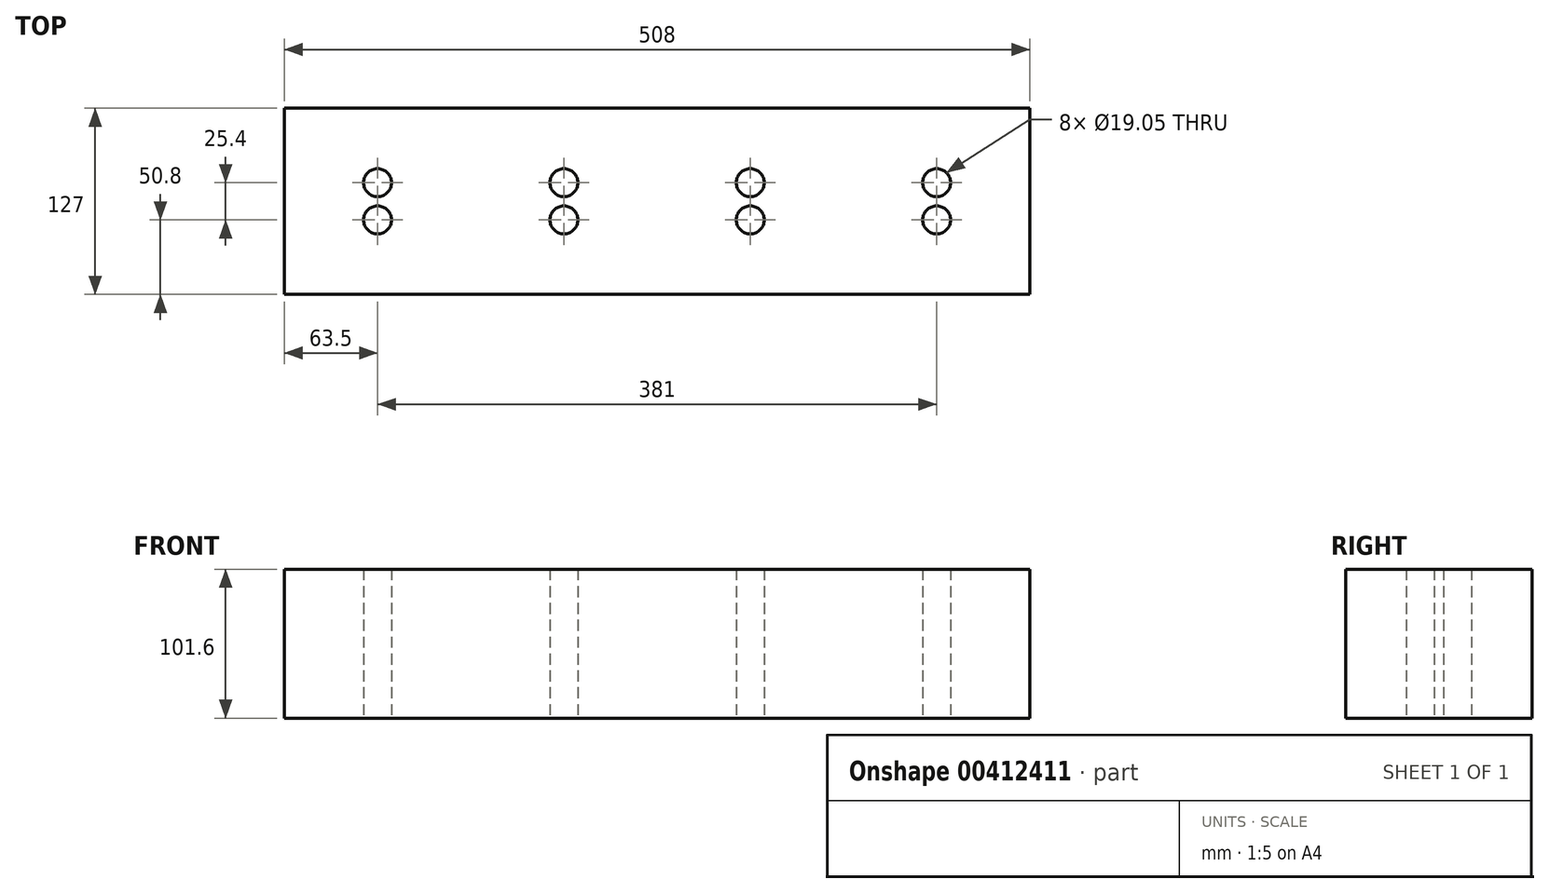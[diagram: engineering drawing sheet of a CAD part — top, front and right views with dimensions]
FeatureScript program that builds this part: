
annotation { "Feature Type Name" : "Feature", "Feature Type Description" : "" }
export const myFeature = defineFeature(function(context is Context, id is Id, definition is map)
    precondition{}
    {
        {
            var Q0;
            Q0=qCreatedBy(makeId("Top.planeOp"),FACE);
            var sketch = newSketch(context, id + "F0", { "sketchPlane" : qUnion([Q0])});
            skLineSegment(sketch, "E0", {"start": v(0, 0) * mm, "end": v(508, 0) * mm});
            skLineSegment(sketch, "E1", {"start": v(0, 127) * mm, "end": v(0, 0) * mm});
            skLineSegment(sketch, "E2", {"start": v(508, 127) * mm, "end": v(0, 127) * mm});
            skLineSegment(sketch, "E3", {"start": v(508, 127) * mm, "end": v(508, 0) * mm});
            skCircle(sketch, "E4", {"center": v(63.5, 76.2) * mm, "radius": 9.53 * mm});
            skCircle(sketch, "E5", {"center": v(63.5, 50.8) * mm, "radius": 9.53 * mm});
            skCircle(sketch, "E6", {"center": v(190.5, 76.2) * mm, "radius": 9.53 * mm});
            skCircle(sketch, "E7", {"center": v(190.5, 50.8) * mm, "radius": 9.53 * mm});
            skCircle(sketch, "E8", {"center": v(317.5, 76.2) * mm, "radius": 9.53 * mm});
            skCircle(sketch, "E9", {"center": v(317.5, 50.8) * mm, "radius": 9.53 * mm});
            skCircle(sketch, "E10", {"center": v(444.5, 76.2) * mm, "radius": 9.53 * mm});
            skCircle(sketch, "E11", {"center": v(444.5, 50.8) * mm, "radius": 9.53 * mm});
            skSolve(sketch);
        }
        {
            var Q0;
            Q0=makeQuery(id+"F0.imprint","IMPRINT",FACE,{"disambiguationData":[TD([[makeQuery(id+"F0.imprint","IMPRINT",EDGE,{"derivedFrom":sQuery(id+"F0.wireOp",EDGE,"E0")}),1.0]])]});
            var Q1;
            Q1 = qSketchRegion(id + "F0", true);
            extrude(context, id + "F1", {"entities" : qUnion([Q0, Q1]), "depth" : 25.4 * mm});
        }
        {
            var Q0;
            Q0=makeQuery(id+"F1.opExtrude","CAP_EDGE",EDGE,{"disambiguationData":[OSD([sQuery(id+"F0.wireOp",EDGE,"E6")])],"isStart":false});
            var Q1;
            Q1=makeQuery(id+"F1.opExtrude","CAP_EDGE",EDGE,{"disambiguationData":[OSD([sQuery(id+"F0.wireOp",EDGE,"E7")])],"isStart":false});
            var Q2;
            Q2=makeQuery(id+"F1.opExtrude","CAP_EDGE",EDGE,{"disambiguationData":[OSD([sQuery(id+"F0.wireOp",EDGE,"E8")])],"isStart":false});
            var Q3;
            Q3=makeQuery(id+"F1.opExtrude","CAP_EDGE",EDGE,{"disambiguationData":[OSD([sQuery(id+"F0.wireOp",EDGE,"E9")])],"isStart":false});
            var Q4;
            Q4=makeQuery(id+"F1.opExtrude","CAP_EDGE",EDGE,{"disambiguationData":[OSD([sQuery(id+"F0.wireOp",EDGE,"E4")])],"isStart":false});
            var Q5;
            Q5=makeQuery(id+"F1.opExtrude","CAP_EDGE",EDGE,{"disambiguationData":[OSD([sQuery(id+"F0.wireOp",EDGE,"E5")])],"isStart":false});
            var Q6;
            Q6=makeQuery(id+"F1.opExtrude","CAP_EDGE",EDGE,{"disambiguationData":[OSD([sQuery(id+"F0.wireOp",EDGE,"E10")])],"isStart":false});
            var Q7;
            Q7=makeQuery(id+"F1.opExtrude","CAP_EDGE",EDGE,{"disambiguationData":[OSD([sQuery(id+"F0.wireOp",EDGE,"E11")])],"isStart":false});
            var Q8;
            Q8=makeQuery(id+"F1.opExtrude","CAP_EDGE",EDGE,{"disambiguationData":[OSD([sQuery(id+"F0.wireOp",EDGE,"E7")])],"isStart":true});
            var Q9;
            Q9=makeQuery(id+"F1.opExtrude","CAP_EDGE",EDGE,{"disambiguationData":[OSD([sQuery(id+"F0.wireOp",EDGE,"E6")])],"isStart":true});
            var Q10;
            Q10=makeQuery(id+"F1.opExtrude","CAP_EDGE",EDGE,{"disambiguationData":[OSD([sQuery(id+"F0.wireOp",EDGE,"E9")])],"isStart":true});
            var Q11;
            Q11=makeQuery(id+"F1.opExtrude","CAP_EDGE",EDGE,{"disambiguationData":[OSD([sQuery(id+"F0.wireOp",EDGE,"E8")])],"isStart":true});
            var Q12;
            Q12=makeQuery(id+"F1.opExtrude","CAP_EDGE",EDGE,{"disambiguationData":[OSD([sQuery(id+"F0.wireOp",EDGE,"E11")])],"isStart":true});
            var Q13;
            Q13=makeQuery(id+"F1.opExtrude","CAP_EDGE",EDGE,{"disambiguationData":[OSD([sQuery(id+"F0.wireOp",EDGE,"E10")])],"isStart":true});
            var Q14;
            Q14=makeQuery(id+"F1.opExtrude","CAP_EDGE",EDGE,{"disambiguationData":[OSD([sQuery(id+"F0.wireOp",EDGE,"E4")])],"isStart":true});
            var Q15;
            Q15=makeQuery(id+"F1.opExtrude","CAP_EDGE",EDGE,{"disambiguationData":[OSD([sQuery(id+"F0.wireOp",EDGE,"E5")])],"isStart":true});
            fillet(context, id + "F2", {"entities" : qUnion([Q0, Q1, Q2, Q3, Q4, Q5, Q6, Q7, Q8, Q9, Q10, Q11, Q12, Q13, Q14, Q15]), "radius" : 5.08 * mm, "tangentPropagation" : true, "allowEdgeOverflow" : false});
        }
        {
            var Q0;
            Q0 = qSketchRegion(id + "F0", true);
            extrude(context, id + "F3", {"entities" : qUnion([Q0]), "operationType" : NewBodyOperationType.ADD, "depth" : 101.6 * mm});
        }
    });
